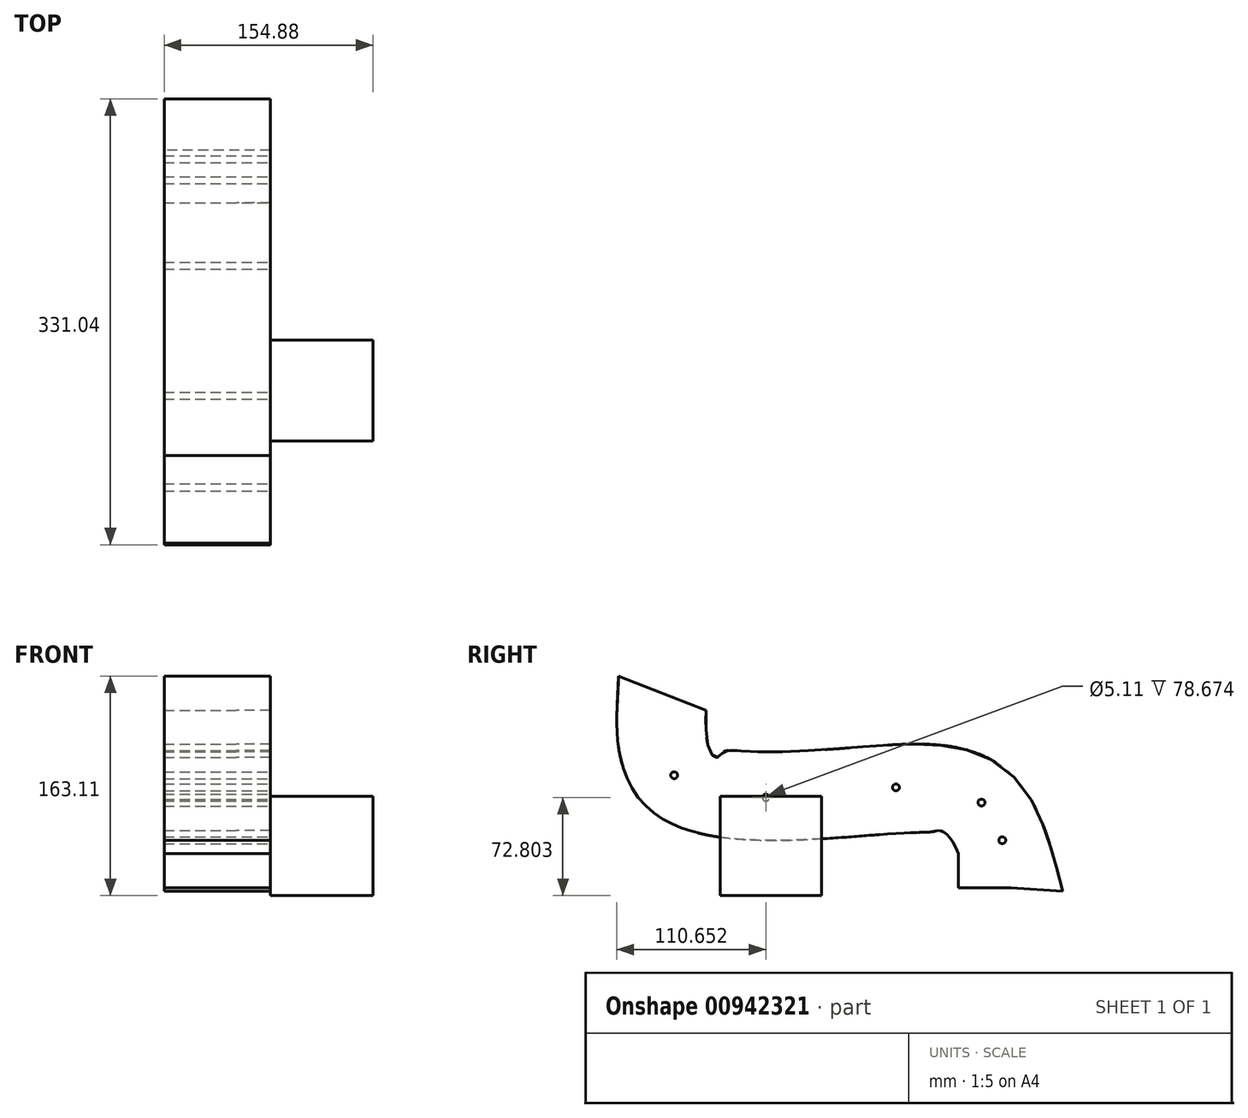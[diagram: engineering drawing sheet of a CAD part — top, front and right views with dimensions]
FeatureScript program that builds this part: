
annotation { "Feature Type Name" : "Feature", "Feature Type Description" : "" }
export const myFeature = defineFeature(function(context is Context, id is Id, definition is map)
    precondition{}
    {
        {
            var Q0;
            Q0=qCreatedBy(makeId("Top.planeOp"),FACE);
            var sketch = newSketch(context, id + "F0", { "sketchPlane" : qUnion([Q0])});
            skLineSegment(sketch, "E0.bottom", {"start": v(-35.38, -39.05) * mm, "end": v(17.9, -39.05) * mm});
            skLineSegment(sketch, "E0.top", {"start": v(-35.38, 30.78) * mm, "end": v(17.9, 30.78) * mm});
            skLineSegment(sketch, "E0.left", {"start": v(-35.38, -39.05) * mm, "end": v(-35.38, 30.78) * mm});
            skLineSegment(sketch, "E0.right", {"start": v(17.9, -39.05) * mm, "end": v(17.9, 30.78) * mm});
            skSolve(sketch);
        }
        {
            var Q0;
            Q0 = qSketchRegion(id + "F0", true);
            extrude(context, id + "F1", {"entities" : qUnion([Q0]), "depth" : 25.4 * mm, "offsetDistance" : 25.4 * mm});
        }
        {
            var Q0;
            Q0=qCreatedBy(makeId("Right.planeOp"),FACE);
            var sketch = newSketch(context, id + "F2", { "sketchPlane" : qUnion([Q0])});
            skFitSpline(sketch, "E1", {"points": [v(0, 0) * mm, v(-28.75, 59.83) * mm, v(-112.96, 68.15) * mm, v(-246.72, 79.72) * mm, v(-262.24, 145.8) * mm], "startDerivative": vector(-90.45, 328.6) * mm, "endDerivative": vector(13.93, 353) * mm});
            skSolve(sketch);
        }
        {
            var Q0;
            Q0=makeQuery(id+"F1.opExtrude","CAP_FACE",FACE,{"disambiguationData":[OSD([sQuery(id+"F0.wireOp",EDGE,"E0.bottom"),sQuery(id+"F0.wireOp",EDGE,"E0.top"),sQuery(id+"F0.wireOp",EDGE,"E0.left"),sQuery(id+"F0.wireOp",EDGE,"E0.right")])],"isStart":false});
            var Q1;
            Q1=sQuery(id+"F2.wireOp",EDGE,"E1");
            sweep(context, id + "F3", {"operationType" : NewBodyOperationType.ADD, "profiles" : qUnion([Q0]), "path" : qUnion([Q1])});
        }
        {
            var Q0;
            Q0=qCreatedBy(makeId("Front.planeOp"),FACE);
            var sketch = newSketch(context, id + "F4", { "sketchPlane" : qUnion([Q0])});
            skLineSegment(sketch, "E2", {"start": v(0, 0) * mm, "end": v(678.3, 85.34) * mm});
            skSolve(sketch);
        }
        {
            var Q0;
            {var subQ0=sQuery(id+"F0.wireOp",EDGE,"E0.right");Q0=makeQuery(id+"F3.boolean.opBoolean","MERGE",FACE,{"derivedFrom":[makeQuery(id+"F1.opExtrude","SWEPT_FACE",FACE,{"disambiguationData":[OSD([subQ0])]}),makeQuery(id+"F3.opSweep","SWEPT_FACE",FACE,{"disambiguationData":[OSD([subQ0,sQuery(id+"F2.wireOp",EDGE,"E1")])]})]});}
            var sketch = newSketch(context, id + "F5", { "sketchPlane" : qUnion([Q0])});
            skPoint(sketch, "E3", {"position": v(-250.21, 83.6) * mm});
            skPoint(sketch, "E4", {"position": v(-182.13, 66.96) * mm});
            skPoint(sketch, "E5", {"position": v(-85.57, 74.53) * mm});
            skPoint(sketch, "E6", {"position": v(-22, 63.3) * mm});
            skPoint(sketch, "E7", {"position": v(-6.61, 35.29) * mm});
            skSolve(sketch);
        }
        {
            var Q0;
            Q0=sQuery(id+"F5.wireOp",VERTEX,"E3");
            var Q1;
            Q1=sQuery(id+"F5.wireOp",VERTEX,"E4");
            var Q2;
            Q2=sQuery(id+"F5.wireOp",VERTEX,"E5");
            var Q3;
            Q3=sQuery(id+"F5.wireOp",VERTEX,"E6");
            var Q4;
            Q4=sQuery(id+"F5.wireOp",VERTEX,"E7");
            var Q5;
            Q5=makeQuery(id+"F1.opExtrude","SWEPT_BODY",BODY,{"disambiguationData":[OSD([sQuery(id+"F0.wireOp",EDGE,"E0.bottom"),sQuery(id+"F0.wireOp",EDGE,"E0.top"),sQuery(id+"F0.wireOp",EDGE,"E0.left"),sQuery(id+"F0.wireOp",EDGE,"E0.right")])]});
            hole(context, id + "F6", {"style" : HoleStyle.SIMPLE, "endStyle" : HoleEndStyle.THROUGH, "standardTappedOrClearance" : lookupTablePath({ "standard" : "ANSI", "engagement" : "75%", "pitch" : "20 tpi", "size" : "1/4", "type" : "Tapped" }), "standardBlindInLast" : lookupTablePath({ "standard" : "ANSI", "fit" : "Normal", "engagement" : "75%", "pitch" : "20 tpi", "size" : "1/4", "type" : "Clearance & tapped" }), "holeDiameter" : 5.1 * mm, "majorDiameter" : 6.35 * mm, "showTappedDepth" : true, "isTappedThrough" : true, "tappedDepth" : 12.7 * mm, "tapClearance" : 3, "locations" : qUnion([Q0, Q1, Q2, Q3, Q4]), "scope" : qUnion([Q5])});
        }
        {
            var Q0;
            {var subQ0=sQuery(id+"F0.wireOp",EDGE,"E0.right");Q0=makeQuery(id+"F3.boolean.opBoolean","MERGE",FACE,{"derivedFrom":[makeQuery(id+"F1.opExtrude","SWEPT_FACE",FACE,{"disambiguationData":[OSD([subQ0])]}),makeQuery(id+"F3.opSweep","SWEPT_FACE",FACE,{"disambiguationData":[OSD([subQ0,sQuery(id+"F2.wireOp",EDGE,"E1")])]})]});}
            extrude(context, id + "F7", {"entities" : qUnion([Q0]), "operationType" : NewBodyOperationType.ADD, "depth" : 25.4 * mm, "offsetDistance" : 25.4 * mm});
        }
        {
            var Q0;
            Q0=makeQuery(id+"F7.opExtrude","CAP_FACE",FACE,{"disambiguationData":[OSD([sQuery(id+"F0.wireOp",EDGE,"E0.right"),sQuery(id+"F2.wireOp",EDGE,"E1")])],"isStart":false});
            var sketch = newSketch(context, id + "F8", { "sketchPlane" : qUnion([Q0])});
            skLineSegment(sketch, "E8.bottom", {"start": v(-215.92, 67.81) * mm, "end": v(-140.7, 67.81) * mm});
            skLineSegment(sketch, "E8.top", {"start": v(-215.92, -5.84) * mm, "end": v(-140.7, -5.84) * mm});
            skLineSegment(sketch, "E8.left", {"start": v(-215.92, 67.81) * mm, "end": v(-215.92, -5.84) * mm});
            skLineSegment(sketch, "E8.right", {"start": v(-140.7, 67.81) * mm, "end": v(-140.7, -5.84) * mm});
            skSolve(sketch);
        }
        {
            var Q0;
            Q0 = qSketchRegion(id + "F8", true);
            extrude(context, id + "F9", {"entities" : qUnion([Q0]), "operationType" : NewBodyOperationType.ADD, "depth" : 76.2 * mm, "offsetDistance" : 25.4 * mm});
        }
    });
